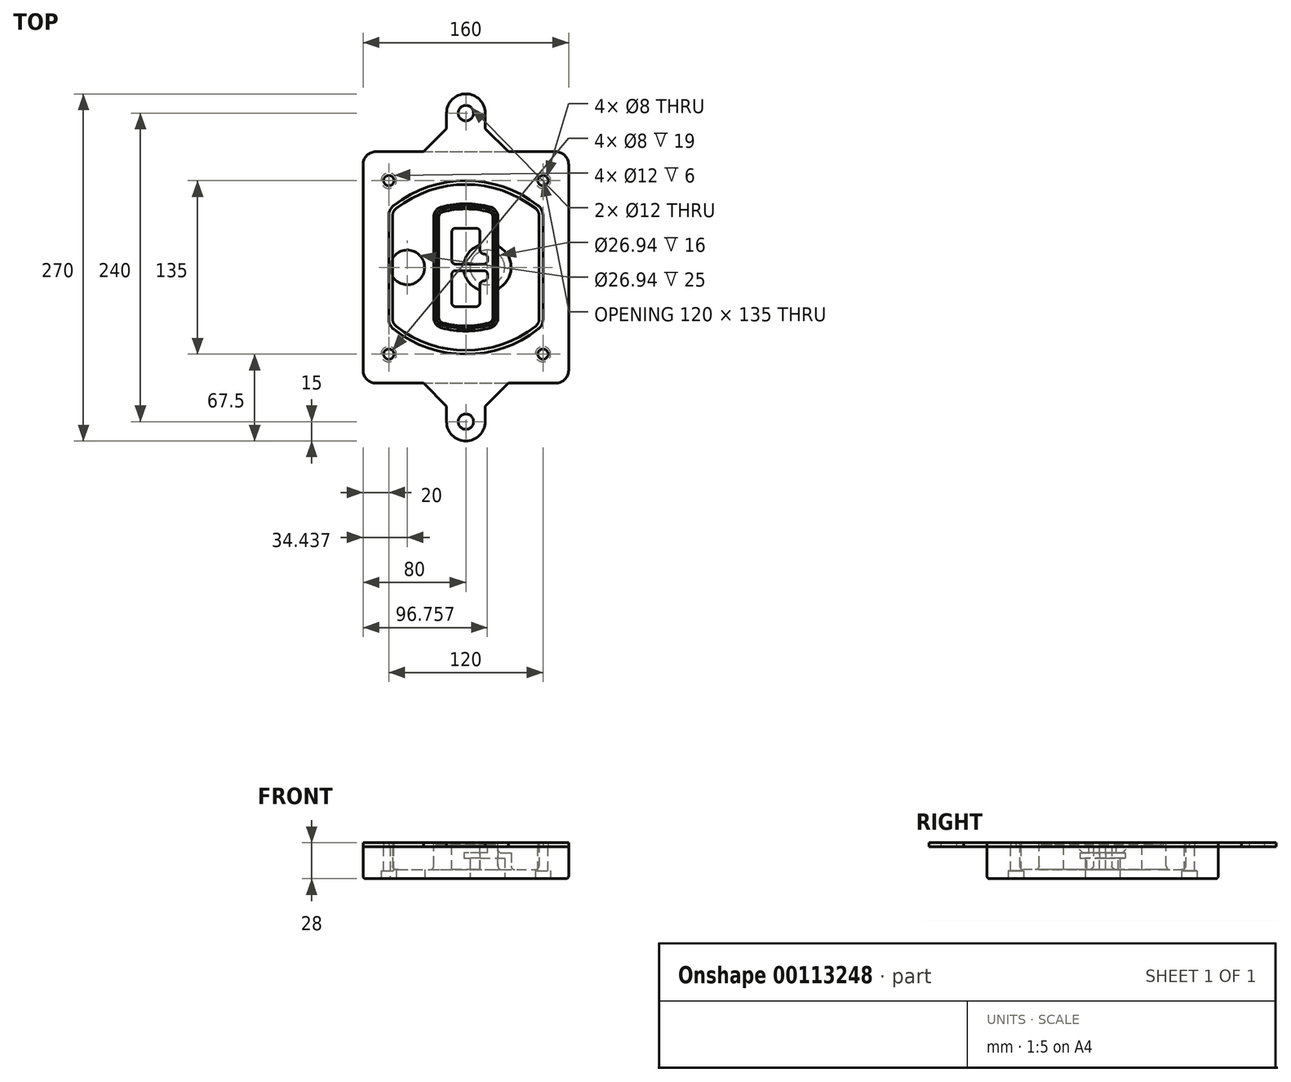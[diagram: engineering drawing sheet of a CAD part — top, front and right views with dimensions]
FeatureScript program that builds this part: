
annotation { "Feature Type Name" : "Feature", "Feature Type Description" : "" }
export const myFeature = defineFeature(function(context is Context, id is Id, definition is map)
    precondition{}
    {
        {
            var Q0;
            Q0=qCreatedBy(makeId("Top.planeOp"),FACE);
            var sketch = newSketch(context, id + "F0", { "sketchPlane" : qUnion([Q0])});
            skPoint(sketch, "E0.rect.middle", {"position": v(0, 0) * mm});
            skLineSegment(sketch, "E1.bottom", {"start": v(-70, -90) * mm, "end": v(70, -90) * mm});
            skLineSegment(sketch, "E1.top", {"start": v(-70, 90) * mm, "end": v(70, 90) * mm});
            skLineSegment(sketch, "E1.left", {"start": v(-80, -80) * mm, "end": v(-80, 80) * mm});
            skLineSegment(sketch, "E1.right", {"start": v(80, -80) * mm, "end": v(80, 80) * mm});
            skLineSegment(sketch, "E2", {"start": v(-80, 90) * mm, "end": v(80, -90) * mm, "construction": true});
            skLineSegment(sketch, "E3", {"start": v(80, 90) * mm, "end": v(-80, -90) * mm, "construction": true});
            skCircle(sketch, "E4", {"center": v(-60, 67.5) * mm, "radius": 4 * mm});
            skCircle(sketch, "E5", {"center": v(60, 67.5) * mm, "radius": 4 * mm});
            skCircle(sketch, "E6", {"center": v(60, -67.5) * mm, "radius": 4 * mm});
            skCircle(sketch, "E7", {"center": v(-60, -67.5) * mm, "radius": 4 * mm});
            skLineSegment(sketch, "E8", {"start": v(-60, 67.5) * mm, "end": v(60, 67.5) * mm, "construction": true});
            skLineSegment(sketch, "E9", {"start": v(60, 67.5) * mm, "end": v(60, -67.5) * mm, "construction": true});
            skLineSegment(sketch, "E10", {"start": v(60, -67.5) * mm, "end": v(-60, -67.5) * mm, "construction": true});
            skLineSegment(sketch, "E11", {"start": v(-60, -67.5) * mm, "end": v(-60, 67.5) * mm, "construction": true});
            skLineSegment(sketch, "E12", {"start": v(-60, 40.3) * mm, "end": v(-60, -40.3) * mm});
            skLineSegment(sketch, "E13", {"start": v(60, 40.3) * mm, "end": v(60, -40.3) * mm});
            skArc(sketch, "E14", {"start": v(56.15, 48.18) * mm, "mid": v(0, 67.5) * mm, "end": v(-56.15, 48.18) * mm});
            skArc(sketch, "E15", {"start": v(-56.15, -48.18) * mm, "mid": v(0, -67.5) * mm, "end": v(56.15, -48.18) * mm});
            skLineSegment(sketch, "E16", {"start": v(-60, 0) * mm, "end": v(60, 0) * mm, "construction": true});
            skPoint(sketch, "E17.visualSharp", {"position": v(-60, -45) * mm});
            skArc(sketch, "E17.filletArc", {"start": v(-60, -40.3) * mm, "mid": v(-58.99, -44.68) * mm, "end": v(-56.15, -48.18) * mm});
            skPoint(sketch, "E18.visualSharp", {"position": v(-60, 45) * mm});
            skArc(sketch, "E18.filletArc", {"start": v(-56.15, 48.18) * mm, "mid": v(-58.99, 44.68) * mm, "end": v(-60, 40.3) * mm});
            skPoint(sketch, "E19.visualSharp", {"position": v(60, 45) * mm});
            skArc(sketch, "E19.filletArc", {"start": v(60, 40.3) * mm, "mid": v(58.99, 44.68) * mm, "end": v(56.15, 48.18) * mm});
            skPoint(sketch, "E20.visualSharp", {"position": v(60, -45) * mm});
            skArc(sketch, "E20.filletArc", {"start": v(56.15, -48.18) * mm, "mid": v(58.99, -44.68) * mm, "end": v(60, -40.3) * mm});
            skPoint(sketch, "E21.visualSharp", {"position": v(-80, 90) * mm});
            skArc(sketch, "E21.filletArc", {"start": v(-70, 90) * mm, "mid": v(-77.07, 87.07) * mm, "end": v(-80, 80) * mm});
            skPoint(sketch, "E22.visualSharp", {"position": v(80, 90) * mm});
            skArc(sketch, "E22.filletArc", {"start": v(80, 80) * mm, "mid": v(77.07, 87.07) * mm, "end": v(70, 90) * mm});
            skPoint(sketch, "E23.visualSharp", {"position": v(80, -90) * mm});
            skArc(sketch, "E23.filletArc", {"start": v(70, -90) * mm, "mid": v(77.07, -87.07) * mm, "end": v(80, -80) * mm});
            skPoint(sketch, "E24.visualSharp", {"position": v(-80, -90) * mm});
            skArc(sketch, "E24.filletArc", {"start": v(-80, -80) * mm, "mid": v(-77.07, -87.07) * mm, "end": v(-70, -90) * mm});
            skArc(sketch, "E25.0", {"start": v(57, 40.3) * mm, "mid": v(56.3, 43.36) * mm, "end": v(54.3, 45.81) * mm});
            skLineSegment(sketch, "E25.1", {"start": v(57, 40.3) * mm, "end": v(57, -40.3) * mm});
            skArc(sketch, "E25.2", {"start": v(54.3, -45.81) * mm, "mid": v(56.3, -43.36) * mm, "end": v(57, -40.3) * mm});
            skArc(sketch, "E25.3", {"start": v(-54.3, -45.81) * mm, "mid": v(0, -64.5) * mm, "end": v(54.3, -45.81) * mm});
            skArc(sketch, "E25.4", {"start": v(-57, -40.3) * mm, "mid": v(-56.3, -43.36) * mm, "end": v(-54.3, -45.81) * mm});
            skArc(sketch, "E25.5", {"start": v(54.3, 45.81) * mm, "mid": v(0, 64.5) * mm, "end": v(-54.3, 45.81) * mm});
            skLineSegment(sketch, "E25.6", {"start": v(-57, 40.3) * mm, "end": v(-57, -40.3) * mm});
            skArc(sketch, "E25.7", {"start": v(-54.3, 45.81) * mm, "mid": v(-56.3, 43.36) * mm, "end": v(-57, 40.3) * mm});
            skArc(sketch, "E26.0", {"start": v(-58.62, 51.33) * mm, "mid": v(-62.58, 46.43) * mm, "end": v(-64, 40.3) * mm});
            skArc(sketch, "E26.1", {"start": v(58.62, 51.33) * mm, "mid": v(0, 71.5) * mm, "end": v(-58.62, 51.33) * mm});
            skArc(sketch, "E26.2", {"start": v(64, 40.3) * mm, "mid": v(62.58, 46.43) * mm, "end": v(58.62, 51.33) * mm});
            skLineSegment(sketch, "E26.3", {"start": v(64, 40.3) * mm, "end": v(64, -40.3) * mm});
            skArc(sketch, "E26.4", {"start": v(58.62, -51.33) * mm, "mid": v(62.58, -46.43) * mm, "end": v(64, -40.3) * mm});
            skLineSegment(sketch, "E26.5", {"start": v(-64, 40.3) * mm, "end": v(-64, -40.3) * mm});
            skArc(sketch, "E26.6", {"start": v(-58.62, -51.33) * mm, "mid": v(0, -71.5) * mm, "end": v(58.62, -51.33) * mm});
            skArc(sketch, "E26.7", {"start": v(-64, -40.3) * mm, "mid": v(-62.58, -46.43) * mm, "end": v(-58.62, -51.33) * mm});
            skSolve(sketch);
        }
        {
            var Q0;
            Q0=makeQuery(id+"F0.imprint","IMPRINT",FACE,{"disambiguationData":[TD([[makeQuery(id+"F0.imprint","IMPRINT",EDGE,{"derivedFrom":sQuery(id+"F0.wireOp",EDGE,"E1.bottom")}),1.0]])]});
            var Q1;
            Q1=makeQuery(id+"F0.imprint","IMPRINT",FACE,{"disambiguationData":[TD([[makeQuery(id+"F0.imprint","IMPRINT",EDGE,{"derivedFrom":sQuery(id+"F0.wireOp",EDGE,"E12")}),1.0]])]});
            var Q2;
            Q2=makeQuery(id+"F0.imprint","IMPRINT",FACE,{"disambiguationData":[TD([[makeQuery(id+"F0.imprint","IMPRINT",EDGE,{"derivedFrom":sQuery(id+"F0.wireOp",EDGE,"E25.0")}),1.0]])]});
            var Q3;
            Q3=makeQuery(id+"F0.imprint","IMPRINT",FACE,{"disambiguationData":[TD([[makeQuery(id+"F0.imprint","IMPRINT",EDGE,{"derivedFrom":sQuery(id+"F0.wireOp",EDGE,"E12")}),-1.0]])]});
            extrude(context, id + "F1", {"entities" : qUnion([Q0, Q1, Q2, Q3]), "oppositeDirection" : true, "depth" : 25 * mm});
        }
        {
            var Q0;
            Q0=makeQuery(id+"F0.imprint","IMPRINT",FACE,{"disambiguationData":[TD([[makeQuery(id+"F0.imprint","IMPRINT",EDGE,{"derivedFrom":sQuery(id+"F0.wireOp",EDGE,"E12")}),1.0]])]});
            extrude(context, id + "F2", {"entities" : qUnion([Q0]), "operationType" : NewBodyOperationType.ADD, "depth" : 3 * mm});
        }
        {
            var Q0;
            Q0=makeQuery(id+"F0.imprint","IMPRINT",FACE,{"disambiguationData":[TD([[makeQuery(id+"F0.imprint","IMPRINT",EDGE,{"derivedFrom":sQuery(id+"F0.wireOp",EDGE,"E25.0")}),1.0]])]});
            extrude(context, id + "F3", {"entities" : qUnion([Q0]), "operationType" : NewBodyOperationType.REMOVE, "oppositeDirection" : true, "depth" : 18 * mm});
        }
        {
            var Q0;
            Q0=makeQuery(id+"F2.opExtrude","CAP_FACE",FACE,{"disambiguationData":[OSD([sQuery(id+"F0.wireOp",EDGE,"E12"),sQuery(id+"F0.wireOp",EDGE,"E13"),sQuery(id+"F0.wireOp",EDGE,"E14"),sQuery(id+"F0.wireOp",EDGE,"E15"),sQuery(id+"F0.wireOp",EDGE,"E17.filletArc"),sQuery(id+"F0.wireOp",EDGE,"E18.filletArc"),sQuery(id+"F0.wireOp",EDGE,"E19.filletArc"),sQuery(id+"F0.wireOp",EDGE,"E20.filletArc"),sQuery(id+"F0.wireOp",EDGE,"E25.0"),sQuery(id+"F0.wireOp",EDGE,"E25.1"),sQuery(id+"F0.wireOp",EDGE,"E25.2"),sQuery(id+"F0.wireOp",EDGE,"E25.3"),sQuery(id+"F0.wireOp",EDGE,"E25.4"),sQuery(id+"F0.wireOp",EDGE,"E25.5"),sQuery(id+"F0.wireOp",EDGE,"E25.6"),sQuery(id+"F0.wireOp",EDGE,"E25.7")])],"isStart":false});
            var sketch = newSketch(context, id + "F4", { "sketchPlane" : qUnion([Q0])});
            skArc(sketch, "E27.0", {"start": v(-19.08, -46.97) * mm, "mid": v(0, -49.5) * mm, "end": v(19.08, -46.97) * mm});
            skArc(sketch, "E28.0", {"start": v(19.08, 46.97) * mm, "mid": v(0, 49.5) * mm, "end": v(-19.08, 46.97) * mm});
            skLineSegment(sketch, "E29", {"start": v(-25, 39.25) * mm, "end": v(-25, -39.25) * mm});
            skLineSegment(sketch, "E30", {"start": v(25, 39.25) * mm, "end": v(25, -39.25) * mm});
            skLineSegment(sketch, "E31", {"start": v(-25, 45.1) * mm, "end": v(25, 45.1) * mm, "construction": true});
            skLineSegment(sketch, "E32", {"start": v(-25, -45.1) * mm, "end": v(25, -45.1) * mm, "construction": true});
            skPoint(sketch, "E33.visualSharp", {"position": v(-25, 45.1) * mm});
            skArc(sketch, "E33.filletArc", {"start": v(-19.08, 46.97) * mm, "mid": v(-23.35, 44.11) * mm, "end": v(-25, 39.25) * mm});
            skPoint(sketch, "E34.visualSharp", {"position": v(25, 45.1) * mm});
            skArc(sketch, "E34.filletArc", {"start": v(25, 39.25) * mm, "mid": v(23.35, 44.11) * mm, "end": v(19.08, 46.97) * mm});
            skPoint(sketch, "E35.visualSharp", {"position": v(25, -45.1) * mm});
            skArc(sketch, "E35.filletArc", {"start": v(19.08, -46.97) * mm, "mid": v(23.35, -44.11) * mm, "end": v(25, -39.25) * mm});
            skPoint(sketch, "E36.visualSharp", {"position": v(-25, -45.1) * mm});
            skArc(sketch, "E36.filletArc", {"start": v(-25, -39.25) * mm, "mid": v(-23.35, -44.11) * mm, "end": v(-19.08, -46.97) * mm});
            skArc(sketch, "E37.0", {"start": v(54.3, 45.81) * mm, "mid": v(0, 64.5) * mm, "end": v(-54.3, 45.81) * mm});
            skArc(sketch, "E37.1", {"start": v(-54.3, 45.81) * mm, "mid": v(-56.3, 43.36) * mm, "end": v(-57, 40.3) * mm});
            skLineSegment(sketch, "E37.2", {"start": v(-57, 40.3) * mm, "end": v(-57, -40.3) * mm});
            skArc(sketch, "E37.3", {"start": v(-57, -40.3) * mm, "mid": v(-56.3, -43.36) * mm, "end": v(-54.3, -45.81) * mm});
            skArc(sketch, "E37.4", {"start": v(-54.3, -45.81) * mm, "mid": v(0, -64.5) * mm, "end": v(54.3, -45.81) * mm});
            skArc(sketch, "E37.5", {"start": v(54.3, -45.81) * mm, "mid": v(56.3, -43.36) * mm, "end": v(57, -40.3) * mm});
            skLineSegment(sketch, "E37.6", {"start": v(57, 40.3) * mm, "end": v(57, -40.3) * mm});
            skArc(sketch, "E37.7", {"start": v(57, 40.3) * mm, "mid": v(56.3, 43.36) * mm, "end": v(54.3, 45.81) * mm});
            skLineSegment(sketch, "E38.0", {"start": v(23, 39.25) * mm, "end": v(23, -39.25) * mm});
            skArc(sketch, "E38.1", {"start": v(18.56, -45.04) * mm, "mid": v(21.76, -42.9) * mm, "end": v(23, -39.25) * mm});
            skArc(sketch, "E38.2", {"start": v(-18.56, -45.04) * mm, "mid": v(0, -47.5) * mm, "end": v(18.56, -45.04) * mm});
            skArc(sketch, "E38.3", {"start": v(-23, -39.25) * mm, "mid": v(-21.76, -42.9) * mm, "end": v(-18.56, -45.04) * mm});
            skLineSegment(sketch, "E38.4", {"start": v(-23, 39.25) * mm, "end": v(-23, -39.25) * mm});
            skArc(sketch, "E38.5", {"start": v(23, 39.25) * mm, "mid": v(21.76, 42.9) * mm, "end": v(18.56, 45.04) * mm});
            skArc(sketch, "E38.6", {"start": v(-18.56, 45.04) * mm, "mid": v(-21.76, 42.9) * mm, "end": v(-23, 39.25) * mm});
            skArc(sketch, "E38.7", {"start": v(18.56, 45.04) * mm, "mid": v(0, 47.5) * mm, "end": v(-18.56, 45.04) * mm});
            skArc(sketch, "E39.0", {"start": v(21, 39.25) * mm, "mid": v(20.18, 41.68) * mm, "end": v(18.04, 43.1) * mm});
            skLineSegment(sketch, "E39.1", {"start": v(21, 39.25) * mm, "end": v(21, -39.25) * mm});
            skArc(sketch, "E39.2", {"start": v(18.04, -43.1) * mm, "mid": v(20.18, -41.68) * mm, "end": v(21, -39.25) * mm});
            skArc(sketch, "E39.3", {"start": v(-18.04, -43.1) * mm, "mid": v(0, -45.5) * mm, "end": v(18.04, -43.1) * mm});
            skArc(sketch, "E39.4", {"start": v(-21, -39.25) * mm, "mid": v(-20.18, -41.68) * mm, "end": v(-18.04, -43.1) * mm});
            skArc(sketch, "E39.5", {"start": v(18.04, 43.1) * mm, "mid": v(0, 45.5) * mm, "end": v(-18.04, 43.1) * mm});
            skLineSegment(sketch, "E39.6", {"start": v(-21, 39.25) * mm, "end": v(-21, -39.25) * mm});
            skArc(sketch, "E39.7", {"start": v(-18.04, 43.1) * mm, "mid": v(-20.18, 41.68) * mm, "end": v(-21, 39.25) * mm});
            skLineSegment(sketch, "E40", {"start": v(-25, 0) * mm, "end": v(25, 0) * mm, "construction": true});
            skLineSegment(sketch, "E41", {"start": v(-11, 5.5) * mm, "end": v(-11, 27.5) * mm});
            skLineSegment(sketch, "E42", {"start": v(-8, 30.5) * mm, "end": v(8, 30.5) * mm});
            skLineSegment(sketch, "E43", {"start": v(11, 27.5) * mm, "end": v(11, 13.5) * mm});
            skLineSegment(sketch, "E44", {"start": v(14, 10.5) * mm, "end": v(14, 10.5) * mm});
            skLineSegment(sketch, "E45", {"start": v(17, 7.5) * mm, "end": v(17, 5.5) * mm});
            skLineSegment(sketch, "E46", {"start": v(14, 2.5) * mm, "end": v(-8, 2.5) * mm});
            skPoint(sketch, "E47.visualSharp", {"position": v(-11, 30.5) * mm});
            skArc(sketch, "E47.filletArc", {"start": v(-8, 30.5) * mm, "mid": v(-10.12, 29.62) * mm, "end": v(-11, 27.5) * mm});
            skPoint(sketch, "E48.visualSharp", {"position": v(11, 30.5) * mm});
            skArc(sketch, "E48.filletArc", {"start": v(11, 27.5) * mm, "mid": v(10.12, 29.62) * mm, "end": v(8, 30.5) * mm});
            skPoint(sketch, "E49.visualSharp", {"position": v(11, 10.5) * mm});
            skArc(sketch, "E49.filletArc", {"start": v(11, 13.5) * mm, "mid": v(11.88, 11.38) * mm, "end": v(14, 10.5) * mm});
            skPoint(sketch, "E50.visualSharp", {"position": v(17, 10.5) * mm});
            skArc(sketch, "E50.filletArc", {"start": v(17, 7.5) * mm, "mid": v(16.12, 9.62) * mm, "end": v(14, 10.5) * mm});
            skPoint(sketch, "E51.visualSharp", {"position": v(17, 2.5) * mm});
            skArc(sketch, "E51.filletArc", {"start": v(14, 2.5) * mm, "mid": v(16.12, 3.38) * mm, "end": v(17, 5.5) * mm});
            skPoint(sketch, "E52.visualSharp", {"position": v(-11, 2.5) * mm});
            skArc(sketch, "E52.filletArc", {"start": v(-11, 5.5) * mm, "mid": v(-10.12, 3.38) * mm, "end": v(-8, 2.5) * mm});
            skLineSegment(sketch, "E53.0.MirrorCS", {"start": v(14, -2.5) * mm, "end": v(-8, -2.5) * mm});
            skArc(sketch, "E54.0.MirrorCS", {"start": v(-11, -5.5) * mm, "mid": v(-10.12, -3.38) * mm, "end": v(-8, -2.5) * mm});
            skLineSegment(sketch, "E55.0.MirrorCS", {"start": v(-11, -5.5) * mm, "end": v(-11, -27.5) * mm});
            skArc(sketch, "E56.0.MirrorCS", {"start": v(-8, -30.5) * mm, "mid": v(-10.12, -29.62) * mm, "end": v(-11, -27.5) * mm});
            skLineSegment(sketch, "E57.0.MirrorCS", {"start": v(-8, -30.5) * mm, "end": v(8, -30.5) * mm});
            skArc(sketch, "E58.0.MirrorCS", {"start": v(11, -27.5) * mm, "mid": v(10.12, -29.62) * mm, "end": v(8, -30.5) * mm});
            skLineSegment(sketch, "E59.0.MirrorCS", {"start": v(11, -27.5) * mm, "end": v(11, -13.5) * mm});
            skArc(sketch, "E60.0.MirrorCS", {"start": v(11, -13.5) * mm, "mid": v(11.88, -11.38) * mm, "end": v(14, -10.5) * mm});
            skArc(sketch, "E61.0.MirrorCS", {"start": v(17, -7.5) * mm, "mid": v(16.12, -9.62) * mm, "end": v(14, -10.5) * mm});
            skLineSegment(sketch, "E62.0.MirrorCS", {"start": v(17, -7.5) * mm, "end": v(17, -5.5) * mm});
            skArc(sketch, "E63.0.MirrorCS", {"start": v(14, -2.5) * mm, "mid": v(16.12, -3.38) * mm, "end": v(17, -5.5) * mm});
            skSolve(sketch);
        }
        {
            var Q0;
            Q0=makeQuery(id+"F4.imprint","IMPRINT",FACE,{"disambiguationData":[TD([[makeQuery(id+"F4.imprint","IMPRINT",EDGE,{"derivedFrom":sQuery(id+"F4.wireOp",EDGE,"E27.0")}),1.0]])]});
            var Q1;
            Q1=makeQuery(id+"F4.imprint","IMPRINT",FACE,{"disambiguationData":[TD([[makeQuery(id+"F4.imprint","IMPRINT",EDGE,{"derivedFrom":sQuery(id+"F4.wireOp",EDGE,"E38.0")}),-1.0]])]});
            var Q2;
            Q2=makeQuery(id+"F4.imprint","IMPRINT",FACE,{"disambiguationData":[TD([[makeQuery(id+"F4.imprint","IMPRINT",EDGE,{"derivedFrom":sQuery(id+"F4.wireOp",EDGE,"E39.0")}),1.0]])]});
            extrude(context, id + "F5", {"entities" : qUnion([Q0, Q1, Q2]), "operationType" : NewBodyOperationType.ADD, "endBound" : BoundingType.UP_TO_NEXT, "oppositeDirection" : true, "depth" : 25 * mm});
        }
        {
            var Q0;
            Q0=makeQuery(id+"F4.imprint","IMPRINT",FACE,{"disambiguationData":[TD([[makeQuery(id+"F4.imprint","IMPRINT",EDGE,{"derivedFrom":sQuery(id+"F4.wireOp",EDGE,"E38.0")}),-1.0]])]});
            extrude(context, id + "F6", {"entities" : qUnion([Q0]), "operationType" : NewBodyOperationType.REMOVE, "oppositeDirection" : true, "depth" : 2 * mm});
        }
        {
            var Q0;
            Q0=makeQuery(id+"F1.opExtrude","CAP_FACE",FACE,{"disambiguationData":[OSD([sQuery(id+"F0.wireOp",EDGE,"E1.bottom"),sQuery(id+"F0.wireOp",EDGE,"E1.top"),sQuery(id+"F0.wireOp",EDGE,"E1.left"),sQuery(id+"F0.wireOp",EDGE,"E1.right"),sQuery(id+"F0.wireOp",EDGE,"E4"),sQuery(id+"F0.wireOp",EDGE,"E5"),sQuery(id+"F0.wireOp",EDGE,"E6"),sQuery(id+"F0.wireOp",EDGE,"E7"),sQuery(id+"F0.wireOp",EDGE,"E21.filletArc"),sQuery(id+"F0.wireOp",EDGE,"E22.filletArc"),sQuery(id+"F0.wireOp",EDGE,"E23.filletArc"),sQuery(id+"F0.wireOp",EDGE,"E24.filletArc")])],"isStart":false});
            var sketch = newSketch(context, id + "F7", { "sketchPlane" : qUnion([Q0])});
            skCircle(sketch, "E64", {"center": v(16.76, 0) * mm, "radius": 13.47 * mm});
            skCircle(sketch, "E65", {"center": v(-45.56, 0) * mm, "radius": 13.47 * mm});
            skLineSegment(sketch, "E66", {"start": v(80, 0) * mm, "end": v(-80, 0) * mm});
            skCircle(sketch, "E67", {"center": v(16.76, 0) * mm, "radius": 18.47 * mm});
            skCircle(sketch, "E68", {"center": v(60, -67.5) * mm, "radius": 6 * mm});
            skCircle(sketch, "E69", {"center": v(-60, -67.5) * mm, "radius": 6 * mm});
            skCircle(sketch, "E70", {"center": v(-60, 67.5) * mm, "radius": 6 * mm});
            skCircle(sketch, "E71", {"center": v(60, 67.5) * mm, "radius": 6 * mm});
            skSolve(sketch);
        }
        {
            var Q0;
            {var subQ1=sQuery(id+"F7.wireOp",EDGE,"E66");var subQ4=sQuery(id+"F7.wireOp",EDGE,"E64");var subQ6=makeQuery(id+"F7.imprint","INTERSECT",VERTEX,{"disambiguationData":[OD(0.0)],"derivedFrom":[subQ4,subQ1]});Q0=makeQuery(id+"F7.imprint","IMPRINT",FACE,{"disambiguationData":[TD([[makeQuery(id+"F7.imprint","IMPRINT",EDGE,{"disambiguationData":[TD([[subQ6,-1.0]])],"derivedFrom":subQ4}),-1.0]])]});}
            var Q1;
            {var subQ0=sQuery(id+"F7.wireOp",EDGE,"E66");var subQ1=sQuery(id+"F7.wireOp",EDGE,"E64");var subQ3=makeQuery(id+"F7.imprint","INTERSECT",VERTEX,{"disambiguationData":[OD(0.0)],"derivedFrom":[subQ1,subQ0]});Q1=makeQuery(id+"F7.imprint","IMPRINT",FACE,{"disambiguationData":[TD([[makeQuery(id+"F7.imprint","IMPRINT",EDGE,{"disambiguationData":[TD([[subQ3,-1.0]])],"derivedFrom":subQ1}),1.0]])]});}
            var Q2;
            {var subQ0=sQuery(id+"F7.wireOp",EDGE,"E66");var subQ1=sQuery(id+"F7.wireOp",EDGE,"E64");var subQ3=makeQuery(id+"F7.imprint","INTERSECT",VERTEX,{"disambiguationData":[OD(0.0)],"derivedFrom":[subQ1,subQ0]});Q2=makeQuery(id+"F7.imprint","IMPRINT",FACE,{"disambiguationData":[TD([[makeQuery(id+"F7.imprint","IMPRINT",EDGE,{"disambiguationData":[TD([[subQ3,1.0]])],"derivedFrom":subQ1}),1.0]])]});}
            var Q3;
            {var subQ1=sQuery(id+"F7.wireOp",EDGE,"E66");var subQ4=sQuery(id+"F7.wireOp",EDGE,"E64");var subQ6=makeQuery(id+"F7.imprint","INTERSECT",VERTEX,{"disambiguationData":[OD(0.0)],"derivedFrom":[subQ4,subQ1]});Q3=makeQuery(id+"F7.imprint","IMPRINT",FACE,{"disambiguationData":[TD([[makeQuery(id+"F7.imprint","IMPRINT",EDGE,{"disambiguationData":[TD([[subQ6,1.0]])],"derivedFrom":subQ4}),-1.0]])]});}
            extrude(context, id + "F8", {"entities" : qUnion([Q0, Q1, Q2, Q3]), "operationType" : NewBodyOperationType.ADD, "oppositeDirection" : true, "depth" : 20 * mm});
        }
        {
            var Q0;
            {var subQ0=sQuery(id+"F7.wireOp",EDGE,"E66");var subQ1=sQuery(id+"F7.wireOp",EDGE,"E64");var subQ3=makeQuery(id+"F7.imprint","INTERSECT",VERTEX,{"disambiguationData":[OD(0.0)],"derivedFrom":[subQ1,subQ0]});Q0=makeQuery(id+"F7.imprint","IMPRINT",FACE,{"disambiguationData":[TD([[makeQuery(id+"F7.imprint","IMPRINT",EDGE,{"disambiguationData":[TD([[subQ3,-1.0]])],"derivedFrom":subQ1}),1.0]])]});}
            var Q1;
            {var subQ0=sQuery(id+"F7.wireOp",EDGE,"E66");var subQ1=sQuery(id+"F7.wireOp",EDGE,"E64");var subQ3=makeQuery(id+"F7.imprint","INTERSECT",VERTEX,{"disambiguationData":[OD(0.0)],"derivedFrom":[subQ1,subQ0]});Q1=makeQuery(id+"F7.imprint","IMPRINT",FACE,{"disambiguationData":[TD([[makeQuery(id+"F7.imprint","IMPRINT",EDGE,{"disambiguationData":[TD([[subQ3,1.0]])],"derivedFrom":subQ1}),1.0]])]});}
            extrude(context, id + "F9", {"entities" : qUnion([Q0, Q1]), "operationType" : NewBodyOperationType.REMOVE, "oppositeDirection" : true, "depth" : 16 * mm});
        }
        {
            var Q0;
            {var subQ0=sQuery(id+"F7.wireOp",EDGE,"E66");var subQ1=sQuery(id+"F7.wireOp",EDGE,"E65");var subQ3=makeQuery(id+"F7.imprint","INTERSECT",VERTEX,{"disambiguationData":[OD(0.0)],"derivedFrom":[subQ1,subQ0]});Q0=makeQuery(id+"F7.imprint","IMPRINT",FACE,{"disambiguationData":[TD([[makeQuery(id+"F7.imprint","IMPRINT",EDGE,{"disambiguationData":[TD([[subQ3,-1.0]])],"derivedFrom":subQ1}),1.0]])]});}
            var Q1;
            {var subQ0=sQuery(id+"F7.wireOp",EDGE,"E66");var subQ1=sQuery(id+"F7.wireOp",EDGE,"E65");var subQ3=makeQuery(id+"F7.imprint","INTERSECT",VERTEX,{"disambiguationData":[OD(0.0)],"derivedFrom":[subQ1,subQ0]});Q1=makeQuery(id+"F7.imprint","IMPRINT",FACE,{"disambiguationData":[TD([[makeQuery(id+"F7.imprint","IMPRINT",EDGE,{"disambiguationData":[TD([[subQ3,1.0]])],"derivedFrom":subQ1}),1.0]])]});}
            extrude(context, id + "F10", {"entities" : qUnion([Q0, Q1]), "operationType" : NewBodyOperationType.REMOVE, "oppositeDirection" : true, "depth" : 25 * mm});
        }
        {
            var Q0;
            Q0=makeQuery(id+"F7.imprint","IMPRINT",FACE,{"disambiguationData":[TD([[makeQuery(id+"F7.imprint","IMPRINT",EDGE,{"derivedFrom":sQuery(id+"F7.wireOp",EDGE,"E68")}),1.0]])]});
            var Q1;
            Q1=makeQuery(id+"F7.imprint","IMPRINT",FACE,{"disambiguationData":[TD([[makeQuery(id+"F7.imprint","IMPRINT",EDGE,{"derivedFrom":makeQuery(id+"F1.opExtrude","CAP_EDGE",EDGE,{"disambiguationData":[OSD([sQuery(id+"F0.wireOp",EDGE,"E5")])],"isStart":false})}),-1.0]])]});
            var Q2;
            Q2=makeQuery(id+"F7.imprint","IMPRINT",FACE,{"disambiguationData":[TD([[makeQuery(id+"F7.imprint","IMPRINT",EDGE,{"derivedFrom":sQuery(id+"F7.wireOp",EDGE,"E69")}),1.0]])]});
            var Q3;
            Q3=makeQuery(id+"F7.imprint","IMPRINT",FACE,{"disambiguationData":[TD([[makeQuery(id+"F7.imprint","IMPRINT",EDGE,{"derivedFrom":makeQuery(id+"F1.opExtrude","CAP_EDGE",EDGE,{"disambiguationData":[OSD([sQuery(id+"F0.wireOp",EDGE,"E4")])],"isStart":false})}),-1.0]])]});
            var Q4;
            Q4=makeQuery(id+"F7.imprint","IMPRINT",FACE,{"disambiguationData":[TD([[makeQuery(id+"F7.imprint","IMPRINT",EDGE,{"derivedFrom":sQuery(id+"F7.wireOp",EDGE,"E70")}),1.0]])]});
            var Q5;
            Q5=makeQuery(id+"F7.imprint","IMPRINT",FACE,{"disambiguationData":[TD([[makeQuery(id+"F7.imprint","IMPRINT",EDGE,{"derivedFrom":makeQuery(id+"F1.opExtrude","CAP_EDGE",EDGE,{"disambiguationData":[OSD([sQuery(id+"F0.wireOp",EDGE,"E7")])],"isStart":false})}),-1.0]])]});
            var Q6;
            Q6=makeQuery(id+"F7.imprint","IMPRINT",FACE,{"disambiguationData":[TD([[makeQuery(id+"F7.imprint","IMPRINT",EDGE,{"derivedFrom":sQuery(id+"F7.wireOp",EDGE,"E71")}),1.0]])]});
            var Q7;
            Q7=makeQuery(id+"F7.imprint","IMPRINT",FACE,{"disambiguationData":[TD([[makeQuery(id+"F7.imprint","IMPRINT",EDGE,{"derivedFrom":makeQuery(id+"F1.opExtrude","CAP_EDGE",EDGE,{"disambiguationData":[OSD([sQuery(id+"F0.wireOp",EDGE,"E6")])],"isStart":false})}),-1.0]])]});
            extrude(context, id + "F11", {"entities" : qUnion([Q0, Q1, Q2, Q3, Q4, Q5, Q6, Q7]), "operationType" : NewBodyOperationType.REMOVE, "oppositeDirection" : true, "depth" : 6 * mm});
        }
        {
            var Q0;
            Q0=makeQuery(id+"F9.boolean.opBoolean","COPY",FACE,{"derivedFrom":makeQuery(id+"F9.opExtrude","CAP_FACE",FACE,{"disambiguationData":[OSD([sQuery(id+"F7.wireOp",EDGE,"E64")])],"isStart":false})});
            var sketch = newSketch(context, id + "F12", { "sketchPlane" : qUnion([Q0])});
            skArc(sketch, "E72.0", {"start": v(11, 17.55) * mm, "mid": v(2.57, 11.82) * mm, "end": v(-1.54, 2.5) * mm});
            skArc(sketch, "E72.1", {"start": v(-1.54, -2.5) * mm, "mid": v(2.57, -11.82) * mm, "end": v(11, -17.55) * mm});
            skLineSegment(sketch, "E73", {"start": v(-1.54, -2.5) * mm, "end": v(14, -2.5) * mm});
            skLineSegment(sketch, "E74.0", {"start": v(14, 2.5) * mm, "end": v(-1.54, 2.5) * mm});
            skArc(sketch, "E74.1", {"start": v(14, 2.5) * mm, "mid": v(16.12, 3.38) * mm, "end": v(17, 5.5) * mm});
            skLineSegment(sketch, "E74.2", {"start": v(17, 7.5) * mm, "end": v(17, 5.5) * mm});
            skArc(sketch, "E74.3", {"start": v(17, 7.5) * mm, "mid": v(16.12, 9.62) * mm, "end": v(14, 10.5) * mm});
            skArc(sketch, "E74.4", {"start": v(11, 13.5) * mm, "mid": v(11.88, 11.38) * mm, "end": v(14, 10.5) * mm});
            skLineSegment(sketch, "E74.5", {"start": v(11, 17.55) * mm, "end": v(11, 13.5) * mm});
            skLineSegment(sketch, "E74.7", {"start": v(14, -2.5) * mm, "end": v(-1.54, -2.5) * mm});
            skArc(sketch, "E74.8", {"start": v(14, -2.5) * mm, "mid": v(16.12, -3.38) * mm, "end": v(17, -5.5) * mm});
            skLineSegment(sketch, "E74.9", {"start": v(17, -7.5) * mm, "end": v(17, -5.5) * mm});
            skArc(sketch, "E74.10", {"start": v(17, -7.5) * mm, "mid": v(16.12, -9.62) * mm, "end": v(14, -10.5) * mm});
            skArc(sketch, "E74.11", {"start": v(11, -13.5) * mm, "mid": v(11.88, -11.38) * mm, "end": v(14, -10.5) * mm});
            skLineSegment(sketch, "E74.12", {"start": v(11, -17.55) * mm, "end": v(11, -13.5) * mm});
            skPoint(sketch, "E75.orphan", {"position": v(11, -27.5) * mm});
            skPoint(sketch, "E76.orphan", {"position": v(-8, -2.5) * mm});
            skPoint(sketch, "E77.orphan", {"position": v(-8, 2.5) * mm});
            skPoint(sketch, "E78.orphan", {"position": v(11, 27.5) * mm});
            skSolve(sketch);
        }
        {
            var Q0;
            {var subQ7=sQuery(id+"F12.wireOp",EDGE,"E72.0");var subQ14=sQuery(id+"F12.wireOp",EDGE,"E72.1");var subQ16=sQuery(id+"F12.wireOp",EDGE,"E74.1");var subQ18=sQuery(id+"F12.wireOp",EDGE,"E74.8");Q0=qUnion([makeQuery(id+"F12.imprint","IMPRINT",FACE,{"disambiguationData":[TD([[makeQuery(id+"F12.imprint","IMPRINT",EDGE,{"derivedFrom":subQ7}),1.0]])]}),makeQuery(id+"F12.imprint","IMPRINT",FACE,{"disambiguationData":[TD([[makeQuery(id+"F12.imprint","IMPRINT",EDGE,{"derivedFrom":subQ14}),1.0]])]}),makeQuery(id+"F12.imprint","IMPRINT",FACE,{"disambiguationData":[TD([[makeQuery(id+"F12.imprint","IMPRINT",EDGE,{"derivedFrom":subQ16}),1.0]])]}),makeQuery(id+"F12.imprint","IMPRINT",FACE,{"disambiguationData":[TD([[makeQuery(id+"F12.imprint","IMPRINT",EDGE,{"derivedFrom":subQ18}),-1.0]])]})]);}
            var Q1;
            Q1=makeQuery(id+"F5.boolean.opBoolean","SPLIT",FACE,{"disambiguationData":[TD([makeQuery(id+"F5.opExtrude","SWEPT_FACE",FACE,{"disambiguationData":[OSD([sQuery(id+"F4.wireOp",EDGE,"E41")])]})])],"derivedFrom":makeQuery(id+"F3.boolean.opBoolean","COPY",FACE,{"derivedFrom":makeQuery(id+"F3.opExtrude","CAP_FACE",FACE,{"disambiguationData":[OSD([sQuery(id+"F0.wireOp",EDGE,"E25.0"),sQuery(id+"F0.wireOp",EDGE,"E25.1"),sQuery(id+"F0.wireOp",EDGE,"E25.2"),sQuery(id+"F0.wireOp",EDGE,"E25.3"),sQuery(id+"F0.wireOp",EDGE,"E25.4"),sQuery(id+"F0.wireOp",EDGE,"E25.5"),sQuery(id+"F0.wireOp",EDGE,"E25.6"),sQuery(id+"F0.wireOp",EDGE,"E25.7")])],"isStart":false})})});
            extrude(context, id + "F13", {"entities" : qUnion([Q0]), "operationType" : NewBodyOperationType.REMOVE, "endBound" : BoundingType.UP_TO_SURFACE, "endBoundEntityFace" : qUnion([Q1]), "depth" : 25 * mm});
        }
        {
            var Q0;
            Q0=makeQuery(id+"F3.boolean.opBoolean","COPY",EDGE,{"derivedFrom":makeQuery(id+"F3.opExtrude","CAP_EDGE",EDGE,{"disambiguationData":[OSD([sQuery(id+"F0.wireOp",EDGE,"E25.6")])],"isStart":false})});
            var Q1;
            Q1=makeQuery(id+"F8.boolean.opBoolean","INTERSECT",EDGE,{"derivedFrom":[makeQuery(id+"F5.opExtrude","SWEPT_FACE",FACE,{"disambiguationData":[OSD([sQuery(id+"F4.wireOp",EDGE,"E30")])]}),makeQuery(id+"F8.opExtrude","CAP_FACE",FACE,{"disambiguationData":[OSD([sQuery(id+"F7.wireOp",EDGE,"E67")])],"isStart":false})]});
            var Q2;
            Q2=makeQuery(id+"F8.boolean.opBoolean","INTERSECT",EDGE,{"disambiguationData":[OD(1.0)],"derivedFrom":[makeQuery(id+"F5.opExtrude","SWEPT_FACE",FACE,{"disambiguationData":[OSD([sQuery(id+"F4.wireOp",EDGE,"E30")])]}),makeQuery(id+"F8.opExtrude","SWEPT_FACE",FACE,{"disambiguationData":[OSD([sQuery(id+"F7.wireOp",EDGE,"E67")])]})]});
            var Q3;
            {var subQ0=sQuery(id+"F4.wireOp",EDGE,"E30");Q3=makeQuery(id+"F8.boolean.opBoolean","SPLIT",EDGE,{"disambiguationData":[TD([makeQuery(id+"F5.opExtrude","SWEPT_FACE",FACE,{"disambiguationData":[OSD([sQuery(id+"F4.wireOp",EDGE,"E35.filletArc")])]})])],"derivedFrom":makeQuery(id+"F5.opExtrude","CAP_EDGE",EDGE,{"disambiguationData":[OSD([subQ0])],"isStart":false})});}
            var Q4;
            {var subQ0=sQuery(id+"F0.wireOp",EDGE,"E25.7");var subQ1=sQuery(id+"F0.wireOp",EDGE,"E25.1");var subQ2=sQuery(id+"F0.wireOp",EDGE,"E25.6");var subQ3=sQuery(id+"F0.wireOp",EDGE,"E25.5");var subQ4=sQuery(id+"F0.wireOp",EDGE,"E25.4");var subQ5=sQuery(id+"F0.wireOp",EDGE,"E25.0");var subQ6=sQuery(id+"F0.wireOp",EDGE,"E25.2");var subQ7=sQuery(id+"F0.wireOp",EDGE,"E25.3");Q4=makeQuery(id+"F8.boolean.opBoolean","INTERSECT",EDGE,{"derivedFrom":[makeQuery(id+"F5.boolean.opBoolean","SPLIT",FACE,{"disambiguationData":[TD([makeQuery(id+"F2.opExtrude","SWEPT_FACE",FACE,{"disambiguationData":[OSD([subQ5])]})])],"derivedFrom":makeQuery(id+"F3.boolean.opBoolean","COPY",FACE,{"derivedFrom":makeQuery(id+"F3.opExtrude","CAP_FACE",FACE,{"disambiguationData":[OSD([subQ5,subQ1,subQ6,subQ7,subQ4,subQ3,subQ2,subQ0])],"isStart":false})})}),makeQuery(id+"F8.opExtrude","SWEPT_FACE",FACE,{"disambiguationData":[OSD([sQuery(id+"F7.wireOp",EDGE,"E67")])]})]});}
            var Q5;
            Q5=makeQuery(id+"F8.boolean.opBoolean","INTERSECT",EDGE,{"disambiguationData":[OD(0.0)],"derivedFrom":[makeQuery(id+"F5.opExtrude","SWEPT_FACE",FACE,{"disambiguationData":[OSD([sQuery(id+"F4.wireOp",EDGE,"E30")])]}),makeQuery(id+"F8.opExtrude","SWEPT_FACE",FACE,{"disambiguationData":[OSD([sQuery(id+"F7.wireOp",EDGE,"E67")])]})]});
            fillet(context, id + "F14", {"entities" : qUnion([Q0, Q1, Q2, Q3, Q4, Q5]), "radius" : 3 * mm, "tangentPropagation" : true, "allowEdgeOverflow" : false});
        }
        {
            var Q0;
            Q0=makeQuery(id+"F1.opExtrude","CAP_EDGE",EDGE,{"disambiguationData":[OSD([sQuery(id+"F0.wireOp",EDGE,"E1.bottom")])],"isStart":false});
            fillet(context, id + "F15", {"entities" : qUnion([Q0]), "radius" : 2 * mm, "tangentPropagation" : true, "allowEdgeOverflow" : false});
        }
        {
            var Q0;
            {var subQ0=sQuery(id+"F0.wireOp",EDGE,"E22.filletArc");var subQ1=sQuery(id+"F0.wireOp",EDGE,"E7");var subQ2=sQuery(id+"F0.wireOp",EDGE,"E6");var subQ3=sQuery(id+"F0.wireOp",EDGE,"E5");var subQ4=sQuery(id+"F0.wireOp",EDGE,"E4");var subQ5=sQuery(id+"F0.wireOp",EDGE,"E1.bottom");var subQ6=sQuery(id+"F0.wireOp",EDGE,"E21.filletArc");var subQ7=sQuery(id+"F0.wireOp",EDGE,"E1.top");var subQ8=sQuery(id+"F0.wireOp",EDGE,"E1.left");var subQ9=sQuery(id+"F0.wireOp",EDGE,"E1.right");var subQ10=sQuery(id+"F0.wireOp",EDGE,"E23.filletArc");var subQ11=sQuery(id+"F0.wireOp",EDGE,"E24.filletArc");Q0=makeQuery(id+"F2.boolean.opBoolean","SPLIT",FACE,{"disambiguationData":[TD([makeQuery(id+"F1.opExtrude","SWEPT_FACE",FACE,{"disambiguationData":[OSD([subQ5])]})])],"derivedFrom":makeQuery(id+"F1.opExtrude","CAP_FACE",FACE,{"disambiguationData":[OSD([subQ5,subQ7,subQ8,subQ9,subQ4,subQ3,subQ2,subQ1,subQ6,subQ0,subQ10,subQ11])],"isStart":true})});}
            var sketch = newSketch(context, id + "F16", { "sketchPlane" : qUnion([Q0])});
            skCircle(sketch, "E79.0", {"center": v(-60, -67.5) * mm, "radius": 4 * mm});
            skCircle(sketch, "E79.1", {"center": v(-60, 67.5) * mm, "radius": 4 * mm});
            skCircle(sketch, "E79.2", {"center": v(60, 67.5) * mm, "radius": 4 * mm});
            skCircle(sketch, "E79.3", {"center": v(60, -67.5) * mm, "radius": 4 * mm});
            skArc(sketch, "E79.4", {"start": v(70, -90) * mm, "mid": v(77.07, -87.07) * mm, "end": v(80, -80) * mm});
            skLineSegment(sketch, "E79.5", {"start": v(-70, -90) * mm, "end": v(70, -90) * mm});
            skArc(sketch, "E79.6", {"start": v(-80, -80) * mm, "mid": v(-77.07, -87.07) * mm, "end": v(-70, -90) * mm});
            skLineSegment(sketch, "E79.7", {"start": v(-80, -80) * mm, "end": v(-80, 80) * mm});
            skArc(sketch, "E79.8", {"start": v(-70, 90) * mm, "mid": v(-77.07, 87.07) * mm, "end": v(-80, 80) * mm});
            skLineSegment(sketch, "E79.9", {"start": v(-70, 90) * mm, "end": v(70, 90) * mm});
            skArc(sketch, "E79.10", {"start": v(80, 80) * mm, "mid": v(77.07, 87.07) * mm, "end": v(70, 90) * mm});
            skLineSegment(sketch, "E79.11", {"start": v(80, -80) * mm, "end": v(80, 80) * mm});
            skArc(sketch, "E79.12", {"start": v(-56.15, -48.18) * mm, "mid": v(0, -67.5) * mm, "end": v(56.15, -48.18) * mm});
            skArc(sketch, "E79.13", {"start": v(-60, -40.3) * mm, "mid": v(-58.99, -44.68) * mm, "end": v(-56.15, -48.18) * mm});
            skArc(sketch, "E79.14", {"start": v(56.15, -48.18) * mm, "mid": v(58.99, -44.68) * mm, "end": v(60, -40.3) * mm});
            skLineSegment(sketch, "E79.15", {"start": v(60, 40.3) * mm, "end": v(60, -40.3) * mm});
            skArc(sketch, "E79.16", {"start": v(60, 40.3) * mm, "mid": v(58.99, 44.68) * mm, "end": v(56.15, 48.18) * mm});
            skArc(sketch, "E79.17", {"start": v(56.15, 48.18) * mm, "mid": v(0, 67.5) * mm, "end": v(-56.15, 48.18) * mm});
            skArc(sketch, "E79.18", {"start": v(-56.15, 48.18) * mm, "mid": v(-58.99, 44.68) * mm, "end": v(-60, 40.3) * mm});
            skLineSegment(sketch, "E79.19", {"start": v(-60, 40.3) * mm, "end": v(-60, -40.3) * mm});
            skLineSegment(sketch, "E80", {"start": v(0, 90) * mm, "end": v(0, 120) * mm, "construction": true});
            skCircle(sketch, "E81", {"center": v(0, 120) * mm, "radius": 6 * mm});
            skArc(sketch, "E82", {"start": v(15, 120) * mm, "mid": v(0, 135) * mm, "end": v(-15, 120) * mm});
            skLineSegment(sketch, "E83", {"start": v(-15, 120) * mm, "end": v(-15, 108) * mm});
            skLineSegment(sketch, "E84", {"start": v(-15, 108) * mm, "end": v(-33, 90) * mm});
            skLineSegment(sketch, "E85", {"start": v(15, 120) * mm, "end": v(15, 108) * mm});
            skLineSegment(sketch, "E86", {"start": v(15, 108) * mm, "end": v(33, 90) * mm});
            skLineSegment(sketch, "E87", {"start": v(-80, 0) * mm, "end": v(80, 0) * mm, "construction": true});
            skArc(sketch, "E88.MirrorCS", {"start": v(-15, 120) * mm, "mid": v(0, 135) * mm, "end": v(15, 120) * mm});
            skArc(sketch, "E89.MirrorCS", {"start": v(15, -120) * mm, "mid": v(0, -135) * mm, "end": v(-15, -120) * mm});
            skLineSegment(sketch, "E90.MirrorCS", {"start": v(-15, -120) * mm, "end": v(-15, -108) * mm});
            skLineSegment(sketch, "E91.MirrorCS", {"start": v(15, -108) * mm, "end": v(33, -90) * mm});
            skLineSegment(sketch, "E92.MirrorCS", {"start": v(15, -120) * mm, "end": v(15, -108) * mm});
            skArc(sketch, "E93.MirrorCS", {"start": v(-15, -120) * mm, "mid": v(0, -135) * mm, "end": v(15, -120) * mm});
            skLineSegment(sketch, "E94.MirrorCS", {"start": v(-15, -108) * mm, "end": v(-33, -90) * mm});
            skCircle(sketch, "E95.MirrorC", {"center": v(0, -120) * mm, "radius": 6 * mm});
            skLineSegment(sketch, "E96.MirrorCS", {"start": v(0, -90) * mm, "end": v(0, -120) * mm, "construction": true});
            skSolve(sketch);
        }
        {
            var Q0;
            {var subQ1=sQuery(id+"F16.wireOp",EDGE,"E91.MirrorCS");Q0=makeQuery(id+"F16.imprint","IMPRINT",FACE,{"disambiguationData":[TD([[makeQuery(id+"F16.imprint","IMPRINT",EDGE,{"derivedFrom":subQ1}),1.0]])]});}
            var Q1;
            Q1=makeQuery(id+"F16.imprint","IMPRINT",FACE,{"disambiguationData":[TD([[makeQuery(id+"F16.imprint","IMPRINT",EDGE,{"derivedFrom":sQuery(id+"F16.wireOp",EDGE,"E79.0")}),-1.0]])]});
            var Q2;
            {var subQ1=sQuery(id+"F16.wireOp",EDGE,"E84");Q2=makeQuery(id+"F16.imprint","IMPRINT",FACE,{"disambiguationData":[TD([[makeQuery(id+"F16.imprint","IMPRINT",EDGE,{"derivedFrom":subQ1}),1.0]])]});}
            var Q3;
            Q3=makeQuery(id+"F2.opExtrude","CAP_FACE",FACE,{"disambiguationData":[OSD([sQuery(id+"F0.wireOp",EDGE,"E12"),sQuery(id+"F0.wireOp",EDGE,"E13"),sQuery(id+"F0.wireOp",EDGE,"E14"),sQuery(id+"F0.wireOp",EDGE,"E15"),sQuery(id+"F0.wireOp",EDGE,"E17.filletArc"),sQuery(id+"F0.wireOp",EDGE,"E18.filletArc"),sQuery(id+"F0.wireOp",EDGE,"E19.filletArc"),sQuery(id+"F0.wireOp",EDGE,"E20.filletArc"),sQuery(id+"F0.wireOp",EDGE,"E25.0"),sQuery(id+"F0.wireOp",EDGE,"E25.1"),sQuery(id+"F0.wireOp",EDGE,"E25.2"),sQuery(id+"F0.wireOp",EDGE,"E25.3"),sQuery(id+"F0.wireOp",EDGE,"E25.4"),sQuery(id+"F0.wireOp",EDGE,"E25.5"),sQuery(id+"F0.wireOp",EDGE,"E25.6"),sQuery(id+"F0.wireOp",EDGE,"E25.7")])],"isStart":false});
            extrude(context, id + "F17", {"entities" : qUnion([Q0, Q1, Q2]), "endBound" : BoundingType.UP_TO_SURFACE, "endBoundEntityFace" : qUnion([Q3]), "depth" : 25 * mm});
        }
    });
